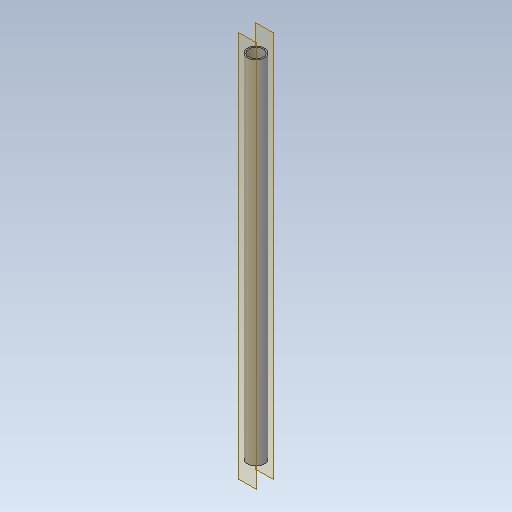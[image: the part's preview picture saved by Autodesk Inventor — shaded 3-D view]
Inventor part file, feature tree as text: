
AUTODESK INVENTOR PART (.ipt)
format: ipt  version: 2020.1 (Build 241239000, 239)  size: 87,552 bytes
history: native  units: mm
features: other x2, extrude x1, sketch x1
ambient origin geometry x8: Origin, YZ Plane, XZ Plane, XY Plane, X Axis, Y Axis, Z Axis, Center Point
bodies: Solid1 (feature_tree)
feature tree (4):
  extrude  "Extrusion1"  Depth=1000.0mm
  other  "rørtangent 1"
  other  "rørtangent 2"
  sketch  "Sketch1"  dims[d0=48.5mm d1=3.75mm d2=41.0mm d3=1000.0mm d4=0.0mm]
